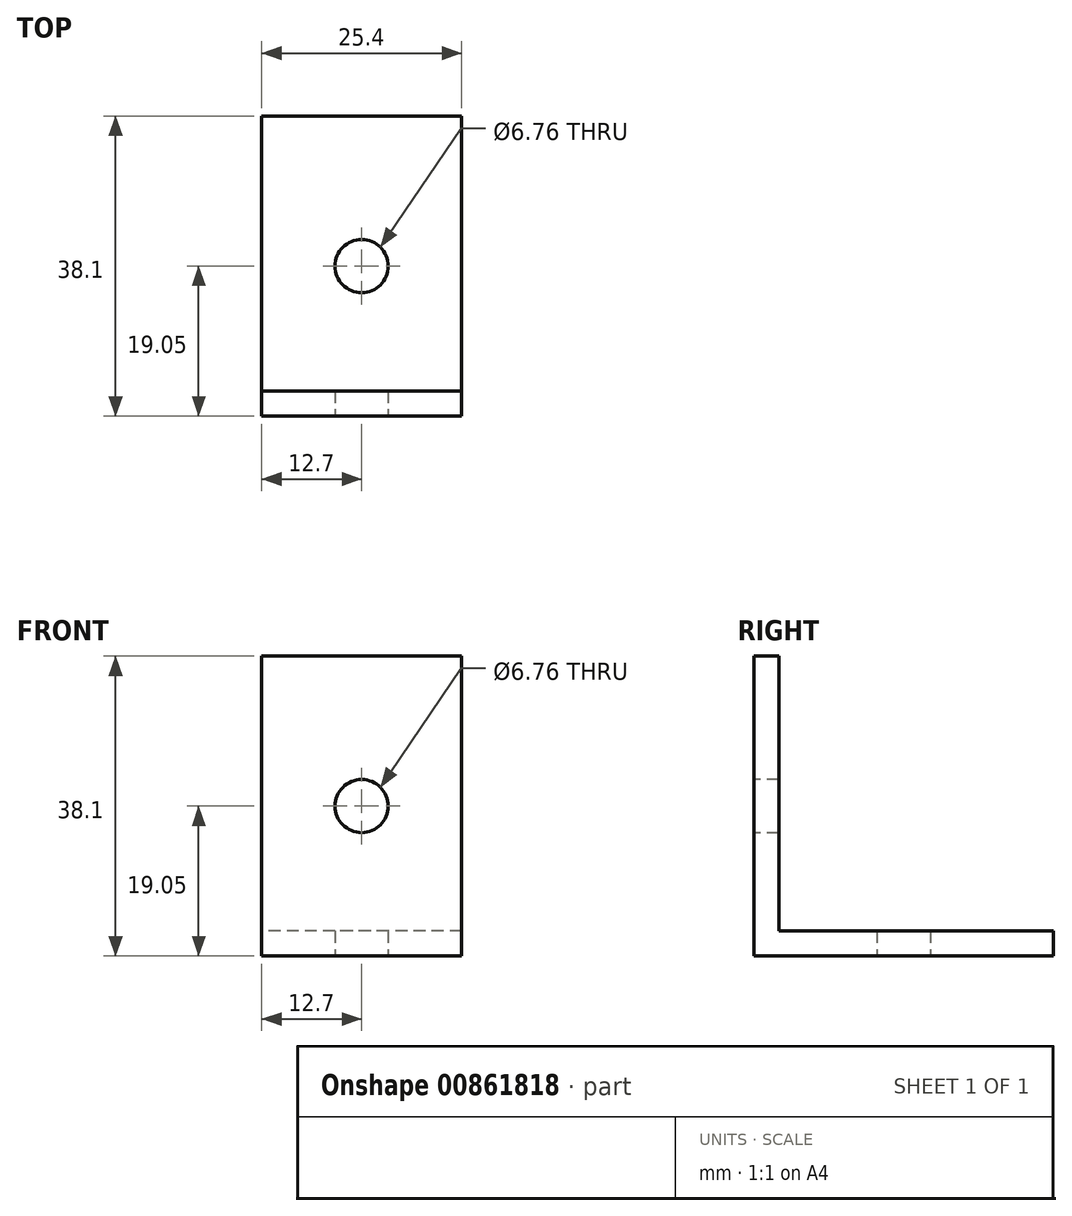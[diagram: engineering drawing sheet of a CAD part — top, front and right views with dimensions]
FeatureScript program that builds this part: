
annotation { "Feature Type Name" : "Feature", "Feature Type Description" : "" }
export const myFeature = defineFeature(function(context is Context, id is Id, definition is map)
    precondition{}
    {
        {
            var Q0;
            Q0=qCreatedBy(makeId("Right.planeOp"),FACE);
            var sketch = newSketch(context, id + "F0", { "sketchPlane" : qUnion([Q0])});
            skLineSegment(sketch, "E0", {"start": v(0, 0) * mm, "end": v(0, 38.1) * mm});
            skLineSegment(sketch, "E1", {"start": v(0, 38.1) * mm, "end": v(3.17, 38.1) * mm});
            skLineSegment(sketch, "E2", {"start": v(3.17, 38.1) * mm, "end": v(3.18, 3.17) * mm});
            skLineSegment(sketch, "E3", {"start": v(3.18, 3.17) * mm, "end": v(38.1, 3.18) * mm});
            skLineSegment(sketch, "E4", {"start": v(38.1, 3.18) * mm, "end": v(38.1, 0) * mm});
            skLineSegment(sketch, "E5", {"start": v(38.1, 0) * mm, "end": v(0, 0) * mm});
            skSolve(sketch);
        }
        {
            var Q0;
            Q0=makeQuery(id+"F0.imprint","IMPRINT",FACE,{"disambiguationData":[TD([[makeQuery(id+"F0.imprint","IMPRINT",EDGE,{"derivedFrom":sQuery(id+"F0.wireOp",EDGE,"E0")}),-1.0]])]});
            extrude(context, id + "F1", {"entities" : qUnion([Q0]), "depth" : 25.4 * mm, "offsetDistance" : 25.4 * mm});
        }
        {
            var Q0;
            Q0=makeQuery(id+"F1.opExtrude","SWEPT_FACE",FACE,{"disambiguationData":[OSD([sQuery(id+"F0.wireOp",EDGE,"E0")])]});
            var sketch = newSketch(context, id + "F2", { "sketchPlane" : qUnion([Q0])});
            skCircle(sketch, "E6", {"center": v(12.7, 19.05) * mm, "radius": 3.38 * mm});
            skSolve(sketch);
        }
        {
            var Q0;
            Q0=makeQuery(id+"F2.imprint","IMPRINT",FACE,{"disambiguationData":[TD([[makeQuery(id+"F2.imprint","IMPRINT",EDGE,{"derivedFrom":sQuery(id+"F2.wireOp",EDGE,"E6")}),1.0]])]});
            extrude(context, id + "F3", {"entities" : qUnion([Q0]), "operationType" : NewBodyOperationType.REMOVE, "oppositeDirection" : true, "depth" : 25.4 * mm, "offsetDistance" : 25.4 * mm});
        }
        {
            var Q0;
            Q0=makeQuery(id+"F1.opExtrude","SWEPT_FACE",FACE,{"disambiguationData":[OSD([sQuery(id+"F0.wireOp",EDGE,"E5")])]});
            var sketch = newSketch(context, id + "F4", { "sketchPlane" : qUnion([Q0])});
            skCircle(sketch, "E7", {"center": v(12.7, -19.05) * mm, "radius": 3.38 * mm});
            skSolve(sketch);
        }
        {
            var Q0;
            Q0=makeQuery(id+"F4.imprint","IMPRINT",FACE,{"disambiguationData":[TD([[makeQuery(id+"F4.imprint","IMPRINT",EDGE,{"derivedFrom":sQuery(id+"F4.wireOp",EDGE,"E7")}),1.0]])]});
            extrude(context, id + "F5", {"entities" : qUnion([Q0]), "operationType" : NewBodyOperationType.REMOVE, "oppositeDirection" : true, "depth" : 25.4 * mm, "offsetDistance" : 25.4 * mm});
        }
    });
